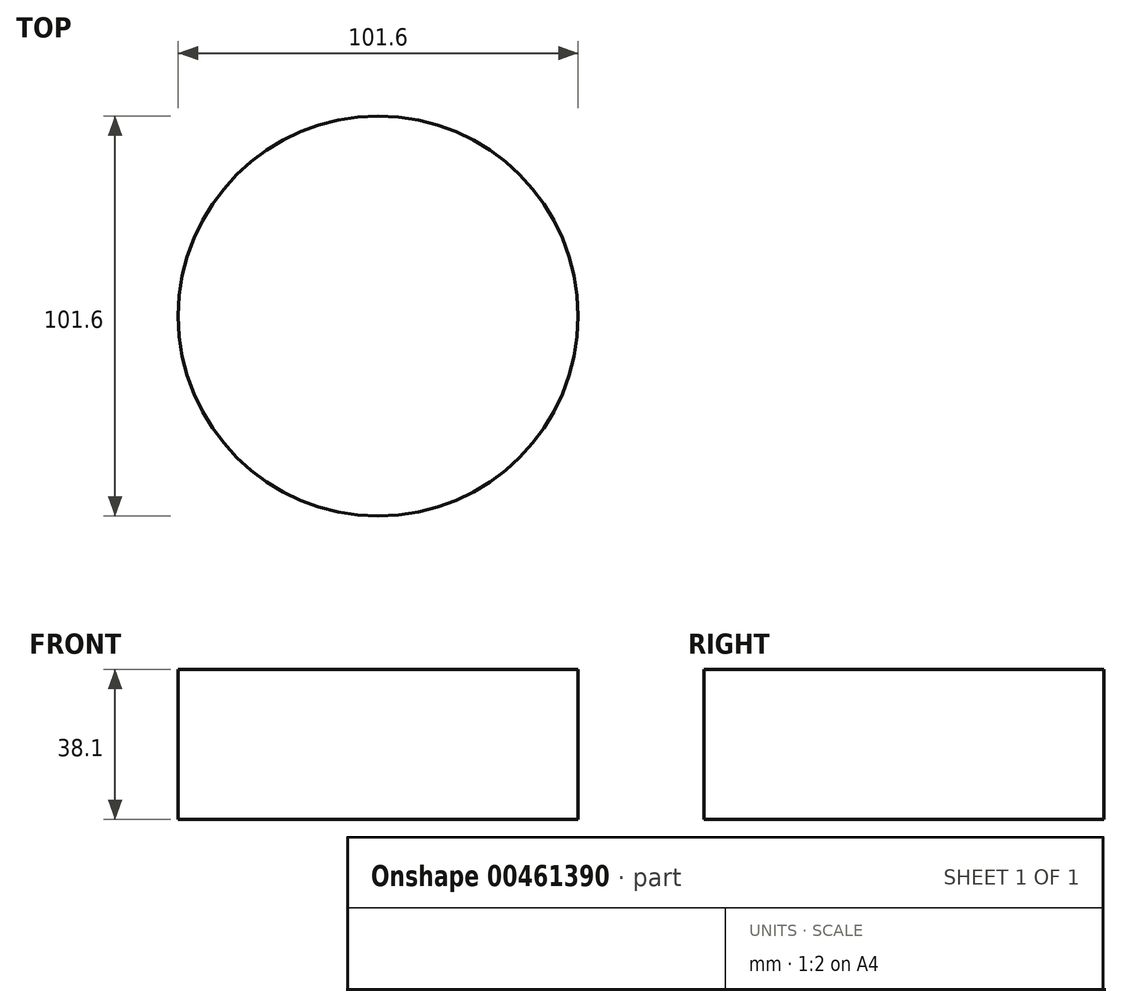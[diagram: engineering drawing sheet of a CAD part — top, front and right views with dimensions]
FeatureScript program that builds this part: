
annotation { "Feature Type Name" : "Feature", "Feature Type Description" : "" }
export const myFeature = defineFeature(function(context is Context, id is Id, definition is map)
    precondition{}
    {
        {
            var Q0;
            Q0=qCreatedBy(makeId("Top.planeOp"),FACE);
            var sketch = newSketch(context, id + "F0", { "sketchPlane" : qUnion([Q0])});
            skCircle(sketch, "E0", {"center": v(0, 0) * mm, "radius": 50.8 * mm});
            skSolve(sketch);
        }
        {
            var Q0;
            Q0 = qSketchRegion(id + "F0", true);
            extrude(context, id + "F1", {"entities" : qUnion([Q0]), "depth" : 38.1 * mm});
        }
    });
